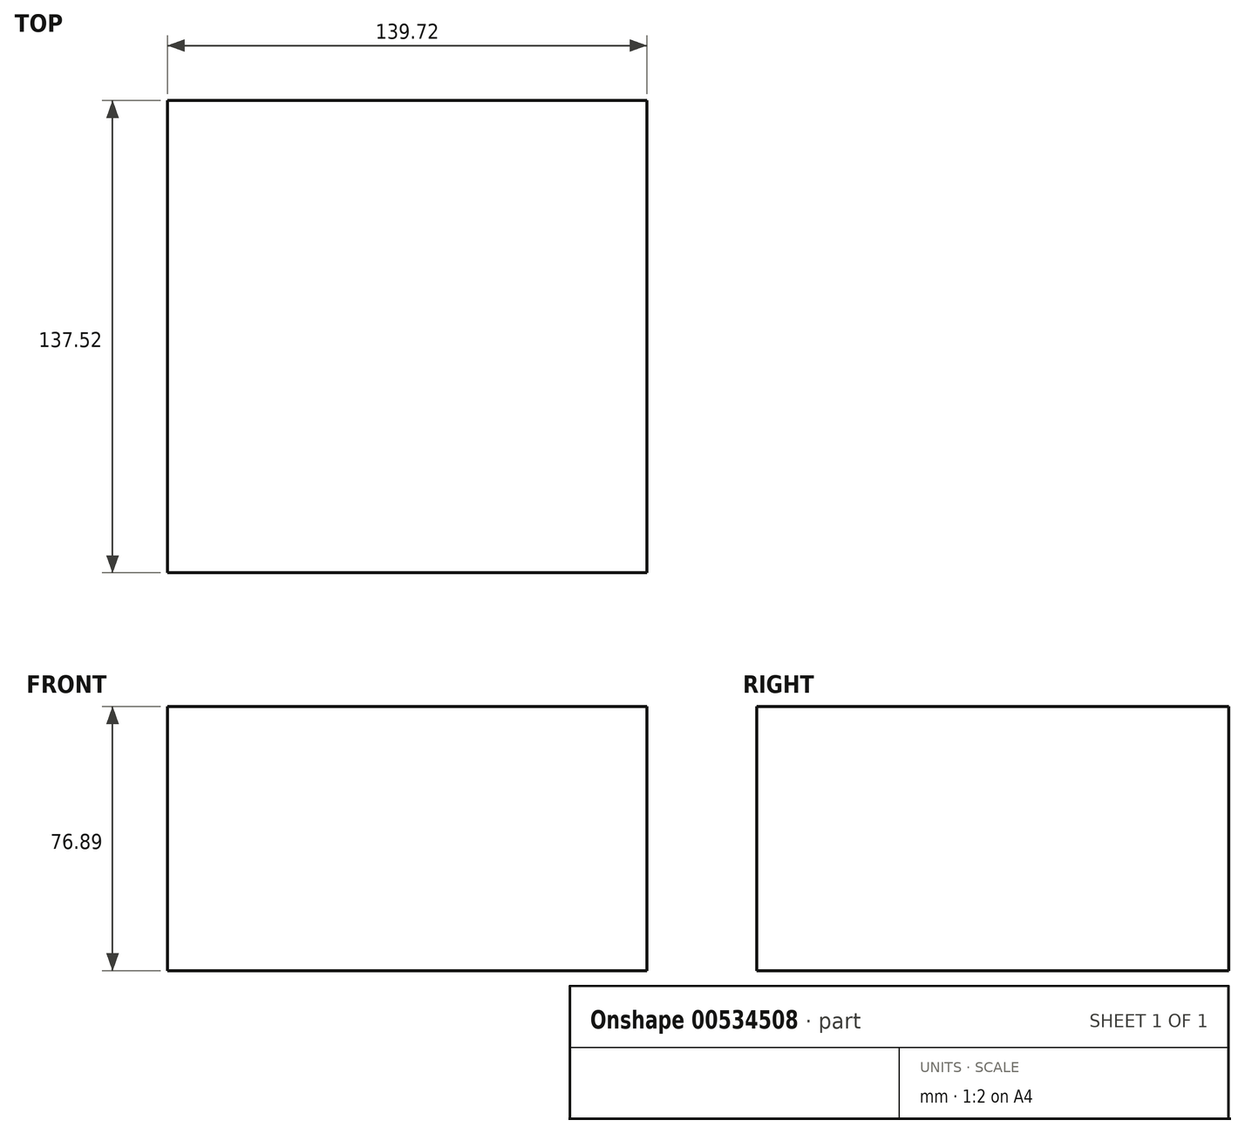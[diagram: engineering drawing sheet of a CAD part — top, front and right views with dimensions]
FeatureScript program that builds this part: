
annotation { "Feature Type Name" : "Feature", "Feature Type Description" : "" }
export const myFeature = defineFeature(function(context is Context, id is Id, definition is map)
    precondition{}
    {
        {
            var Q0;
            Q0=qCreatedBy(makeId("Top.planeOp"),FACE);
            var sketch = newSketch(context, id + "F0", { "sketchPlane" : qUnion([Q0])});
            skLineSegment(sketch, "E0.bottom", {"start": v(69.86, -68.76) * mm, "end": v(-69.86, -68.76) * mm});
            skLineSegment(sketch, "E0.top", {"start": v(69.86, 68.76) * mm, "end": v(-69.86, 68.76) * mm});
            skLineSegment(sketch, "E0.left", {"start": v(69.86, -68.76) * mm, "end": v(69.86, 68.76) * mm});
            skLineSegment(sketch, "E0.right", {"start": v(-69.86, -68.76) * mm, "end": v(-69.86, 68.76) * mm});
            skPoint(sketch, "E0.middle", {"position": v(0, 0) * mm});
            skLineSegment(sketch, "E1", {"start": v(0, 68.76) * mm, "end": v(0, -68.76) * mm});
            skSolve(sketch);
        }
        {
            var Q0;
            Q0=qCreatedBy(makeId("Top.planeOp"),FACE);
            var sketch = newSketch(context, id + "F1", { "sketchPlane" : qUnion([Q0])});
            skCircle(sketch, "E2", {"center": v(54.26, 0) * mm, "radius": 9.82 * mm});
            skSolve(sketch);
        }
        {
            var Q0;
            {var subQ0=sQuery(id+"F0.wireOp",EDGE,"E0.right");Q0=makeQuery(id+"F0.imprint","IMPRINT",FACE,{"disambiguationData":[TD([[makeQuery(id+"F0.imprint","IMPRINT",EDGE,{"derivedFrom":subQ0}),-1.0]])]});}
            var Q1;
            {var subQ0=sQuery(id+"F0.wireOp",EDGE,"E0.left");Q1=makeQuery(id+"F0.imprint","IMPRINT",FACE,{"disambiguationData":[TD([[makeQuery(id+"F0.imprint","IMPRINT",EDGE,{"derivedFrom":subQ0}),1.0]])]});}
            extrude(context, id + "F2", {"entities" : qUnion([Q0, Q1]), "oppositeDirection" : true, "depth" : 76.89 * mm, "offsetDistance" : 25.4 * mm});
        }
        {
            var Q0;
            Q0=sQuery(id+"F1.wireOp",EDGE,"E2");
            var Q1;
            Q1=sQuery(id+"F0.wireOp",EDGE,"E1");
            revolve(context, id + "F3", {"bodyType" : ToolBodyType.SURFACE, "surfaceEntities" : qUnion([Q0]), "axis" : qUnion([Q1]), "revolveType" : RevolveType.FULL});
        }
    });
